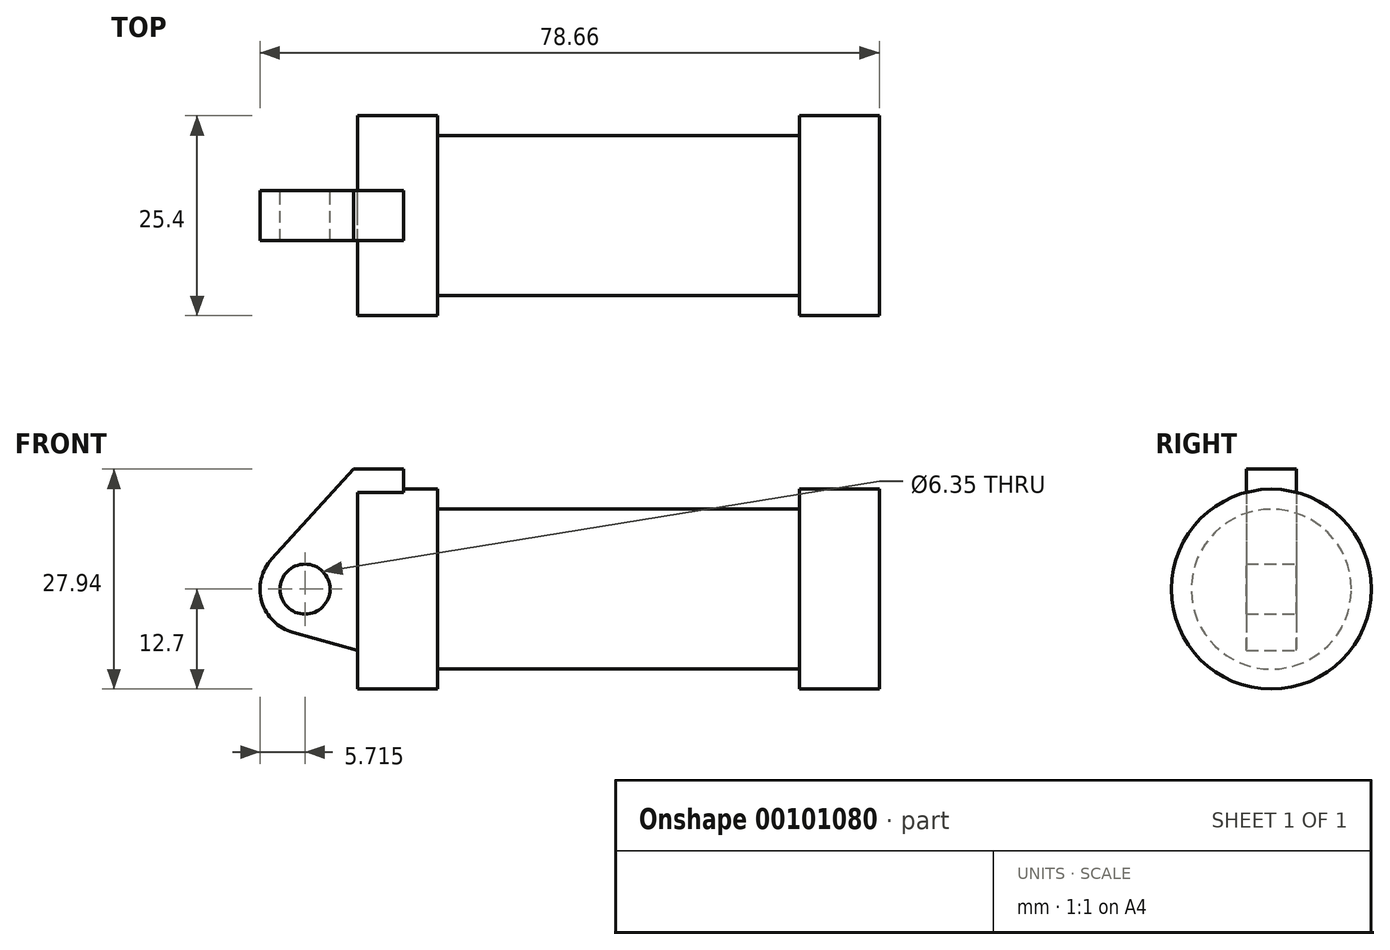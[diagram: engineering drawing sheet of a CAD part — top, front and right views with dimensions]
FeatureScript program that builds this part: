
annotation { "Feature Type Name" : "Feature", "Feature Type Description" : "" }
export const myFeature = defineFeature(function(context is Context, id is Id, definition is map)
    precondition{}
    {
        {
            var Q0;
            Q0=qCreatedBy(makeId("Front.planeOp"),FACE);
            var sketch = newSketch(context, id + "F0", { "sketchPlane" : qUnion([Q0])});
            skLineSegment(sketch, "E0", {"start": v(0, 0) * mm, "end": v(0, 12.7) * mm});
            skLineSegment(sketch, "E1", {"start": v(0, 12.7) * mm, "end": v(10.16, 12.7) * mm});
            skLineSegment(sketch, "E2", {"start": v(10.16, 12.7) * mm, "end": v(10.16, 10.16) * mm});
            skLineSegment(sketch, "E3", {"start": v(10.16, 10.16) * mm, "end": v(56.13, 10.16) * mm});
            skLineSegment(sketch, "E4", {"start": v(56.13, 10.16) * mm, "end": v(56.13, 12.7) * mm});
            skLineSegment(sketch, "E5", {"start": v(56.13, 12.7) * mm, "end": v(66.3, 12.7) * mm});
            skLineSegment(sketch, "E6", {"start": v(66.3, 12.7) * mm, "end": v(66.3, 0) * mm});
            skLineSegment(sketch, "E7", {"start": v(66.3, 0) * mm, "end": v(0, 0) * mm});
            skLineSegment(sketch, "E8", {"start": v(5.84, 15.24) * mm, "end": v(-0.5, 15.24) * mm});
            skLineSegment(sketch, "E9", {"start": v(-0.5, 15.24) * mm, "end": v(-10.88, 3.85) * mm});
            skLineSegment(sketch, "E10", {"start": v(0, 0) * mm, "end": v(-6.65, 0) * mm});
            skCircle(sketch, "E11", {"center": v(-6.65, 0) * mm, "radius": 5.72 * mm});
            skCircle(sketch, "E12", {"center": v(-6.65, 0) * mm, "radius": 3.18 * mm});
            skLineSegment(sketch, "E13", {"start": v(5.84, 15.24) * mm, "end": v(5.84, -9.4) * mm});
            skLineSegment(sketch, "E14", {"start": v(5.84, -9.4) * mm, "end": v(-8.18, -5.5) * mm});
            skSolve(sketch);
        }
        {
            var Q0;
            {var subQ0=sQuery(id+"F0.wireOp",EDGE,"E2");Q0=makeQuery(id+"F0.imprint","IMPRINT",FACE,{"disambiguationData":[TD([[makeQuery(id+"F0.imprint","IMPRINT",EDGE,{"derivedFrom":subQ0}),-1.0]])]});}
            var Q1;
            {var subQ0=sQuery(id+"F0.wireOp",EDGE,"E0");Q1=makeQuery(id+"F0.imprint","IMPRINT",FACE,{"disambiguationData":[TD([[makeQuery(id+"F0.imprint","IMPRINT",EDGE,{"derivedFrom":subQ0}),-1.0]])]});}
            var Q2;
            Q2=sQuery(id+"F0.wireOp",EDGE,"E7");
            revolve(context, id + "F1", {"entities" : qUnion([Q0, Q1]), "axis" : qUnion([Q2]), "revolveType" : RevolveType.FULL});
        }
        {
            var Q0;
            {var subQ3=sQuery(id+"F0.wireOp",EDGE,"E0");Q0=makeQuery(id+"F0.imprint","IMPRINT",FACE,{"disambiguationData":[TD([[makeQuery(id+"F0.imprint","IMPRINT",EDGE,{"derivedFrom":subQ3}),1.0]])]});}
            var Q1;
            {var subQ4=sQuery(id+"F0.wireOp",EDGE,"E12");Q1=makeQuery(id+"F0.imprint","IMPRINT",FACE,{"disambiguationData":[TD([[makeQuery(id+"F0.imprint","IMPRINT",EDGE,{"derivedFrom":subQ4}),-1.0]])]});}
            var Q2;
            {var subQ0=sQuery(id+"F0.wireOp",EDGE,"E14");Q2=makeQuery(id+"F0.imprint","IMPRINT",FACE,{"disambiguationData":[TD([[makeQuery(id+"F0.imprint","IMPRINT",EDGE,{"derivedFrom":subQ0}),-1.0]])]});}
            var Q3;
            {var subQ0=sQuery(id+"F0.wireOp",EDGE,"E0");Q3=makeQuery(id+"F0.imprint","IMPRINT",FACE,{"disambiguationData":[TD([[makeQuery(id+"F0.imprint","IMPRINT",EDGE,{"derivedFrom":subQ0}),-1.0]])]});}
            extrude(context, id + "F2", {"entities" : qUnion([Q0, Q1, Q2, Q3]), "operationType" : NewBodyOperationType.ADD, "endBound" : BoundingType.SYMMETRIC, "depth" : 6.35 * mm});
        }
    });
